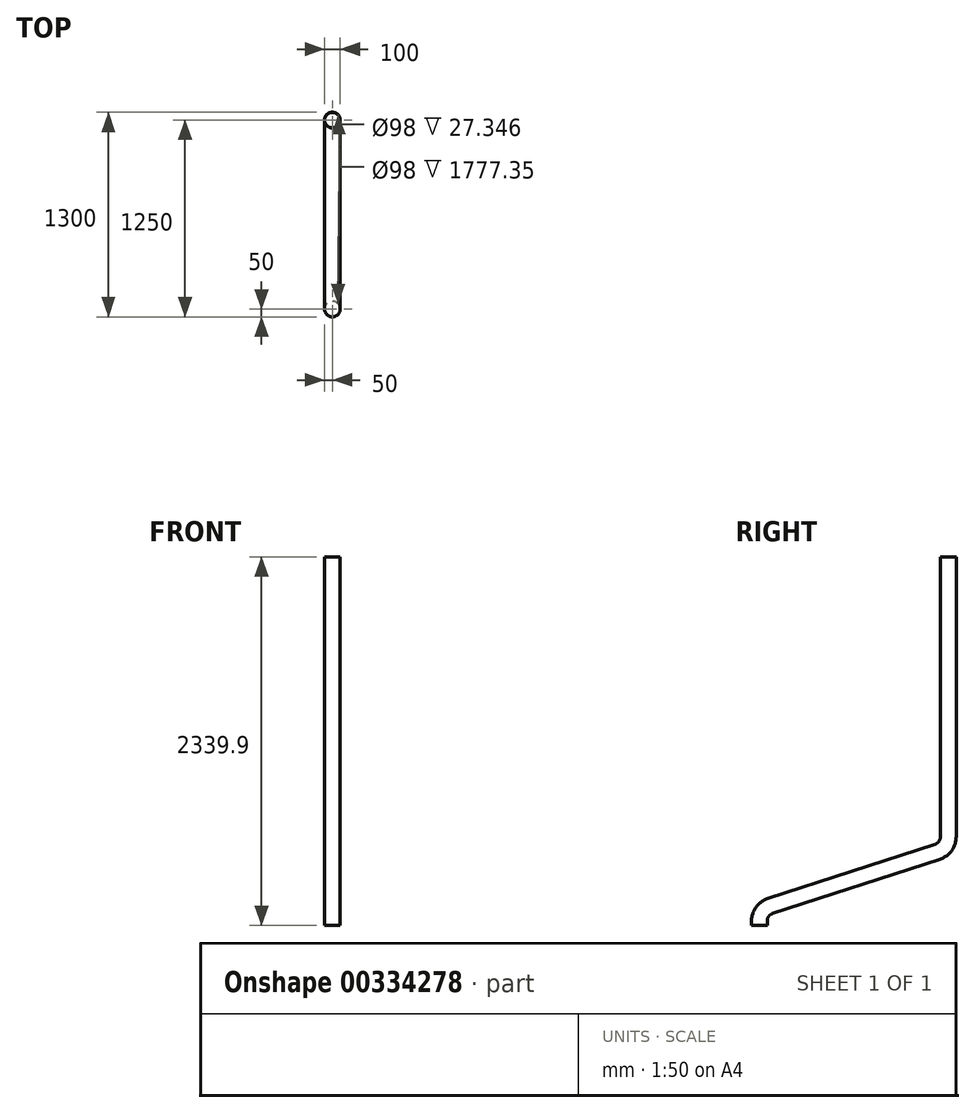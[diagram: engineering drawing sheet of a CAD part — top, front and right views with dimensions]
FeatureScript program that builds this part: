
annotation { "Feature Type Name" : "Feature", "Feature Type Description" : "" }
export const myFeature = defineFeature(function(context is Context, id is Id, definition is map)
    precondition{}
    {
        {
            var Q0;
            Q0=qCreatedBy(makeId("Right.planeOp"),FACE);
            var sketch = newSketch(context, id + "F0", { "sketchPlane" : qUnion([Q0])});
            skLineSegment(sketch, "E0", {"start": v(0, 0) * mm, "end": v(0, -1777.35) * mm});
            skLineSegment(sketch, "E1", {"start": v(-69.1, -1872.45) * mm, "end": v(-1130.9, -2217.45) * mm});
            skLineSegment(sketch, "E2", {"start": v(-1200, -2312.56) * mm, "end": v(-1200, -2339.9) * mm});
            skPoint(sketch, "E3.visualSharp", {"position": v(0, -1850) * mm});
            skArc(sketch, "E3.filletArc", {"start": v(-69.1, -1872.45) * mm, "mid": v(-19.1, -1836.12) * mm, "end": v(0, -1777.35) * mm});
            skPoint(sketch, "E4.visualSharp", {"position": v(-1200, -2239.9) * mm});
            skArc(sketch, "E4.filletArc", {"start": v(-1130.9, -2217.45) * mm, "mid": v(-1180.9, -2253.78) * mm, "end": v(-1200, -2312.56) * mm});
            skSolve(sketch);
        }
        {
            var Q0;
            Q0=qCreatedBy(makeId("Top.planeOp"),FACE);
            var sketch = newSketch(context, id + "F1", { "sketchPlane" : qUnion([Q0])});
            skCircle(sketch, "E5", {"center": v(0, 0) * mm, "radius": 50 * mm});
            skCircle(sketch, "E6", {"center": v(0, 0) * mm, "radius": 49 * mm});
            skSolve(sketch);
        }
        {
            var Q0;
            Q0=makeQuery(id+"F1.imprint","IMPRINT",FACE,{"disambiguationData":[TD([[makeQuery(id+"F1.imprint","IMPRINT",EDGE,{"derivedFrom":sQuery(id+"F1.wireOp",EDGE,"E5")}),1.0]])]});
            var Q1;
            Q1=sQuery(id+"F0.wireOp",EDGE,"E0");
            var Q2;
            Q2=sQuery(id+"F0.wireOp",EDGE,"E3.filletArc");
            var Q3;
            Q3=sQuery(id+"F0.wireOp",EDGE,"E1");
            var Q4;
            Q4=sQuery(id+"F0.wireOp",EDGE,"E4.filletArc");
            var Q5;
            Q5=sQuery(id+"F0.wireOp",EDGE,"E2");
            sweep(context, id + "F2", {"profiles" : qUnion([Q0]), "path" : qUnion([Q1, Q2, Q3, Q4, Q5])});
        }
    });
